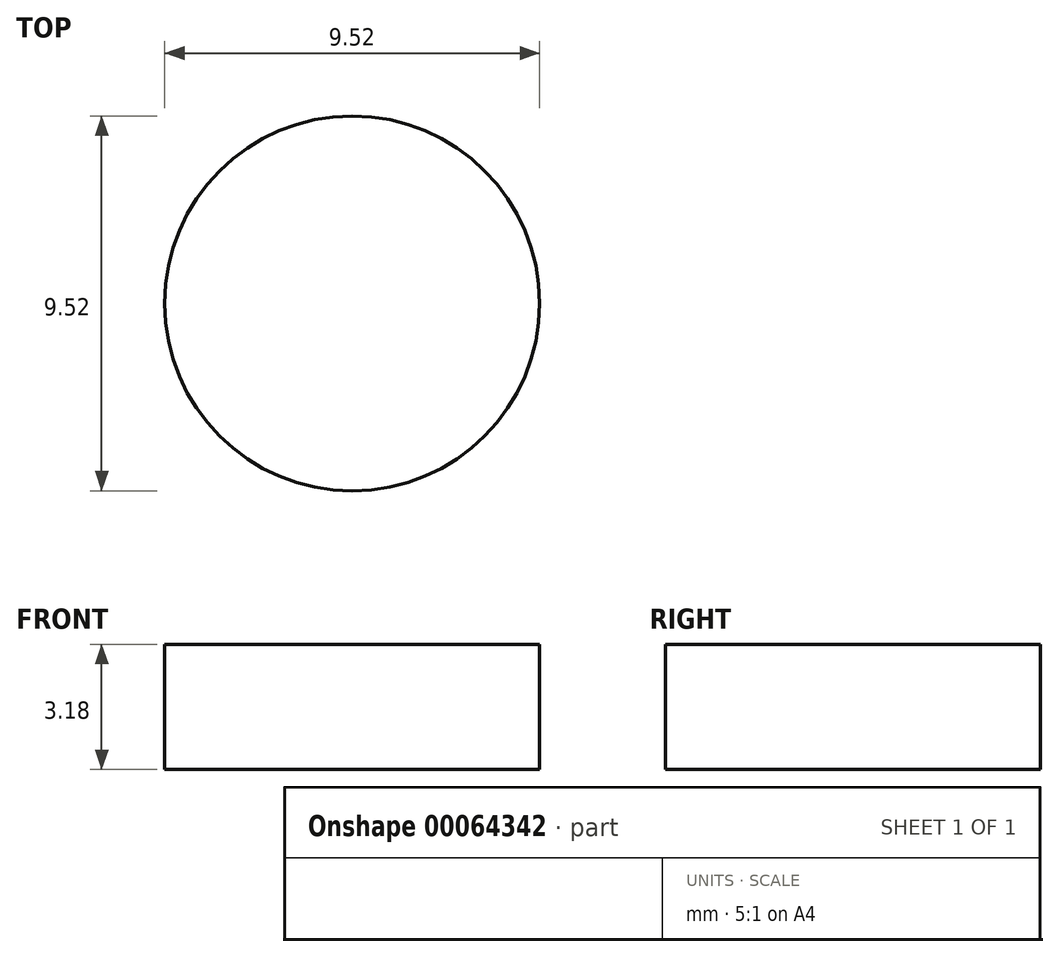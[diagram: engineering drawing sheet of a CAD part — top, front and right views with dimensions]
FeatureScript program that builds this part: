
annotation { "Feature Type Name" : "Feature", "Feature Type Description" : "" }
export const myFeature = defineFeature(function(context is Context, id is Id, definition is map)
    precondition{}
    {
        {
            var Q0;
            Q0=qCreatedBy(makeId("Top.planeOp"),FACE);
            var sketch = newSketch(context, id + "F0", { "sketchPlane" : qUnion([Q0])});
            skCircle(sketch, "E0", {"center": v(0, 0) * mm, "radius": 4.76 * mm});
            skSolve(sketch);
        }
        {
            var Q0;
            Q0 = qSketchRegion(id + "F0", true);
            extrude(context, id + "F1", {"entities" : qUnion([Q0]), "depth" : 3.17 * mm});
        }
    });
